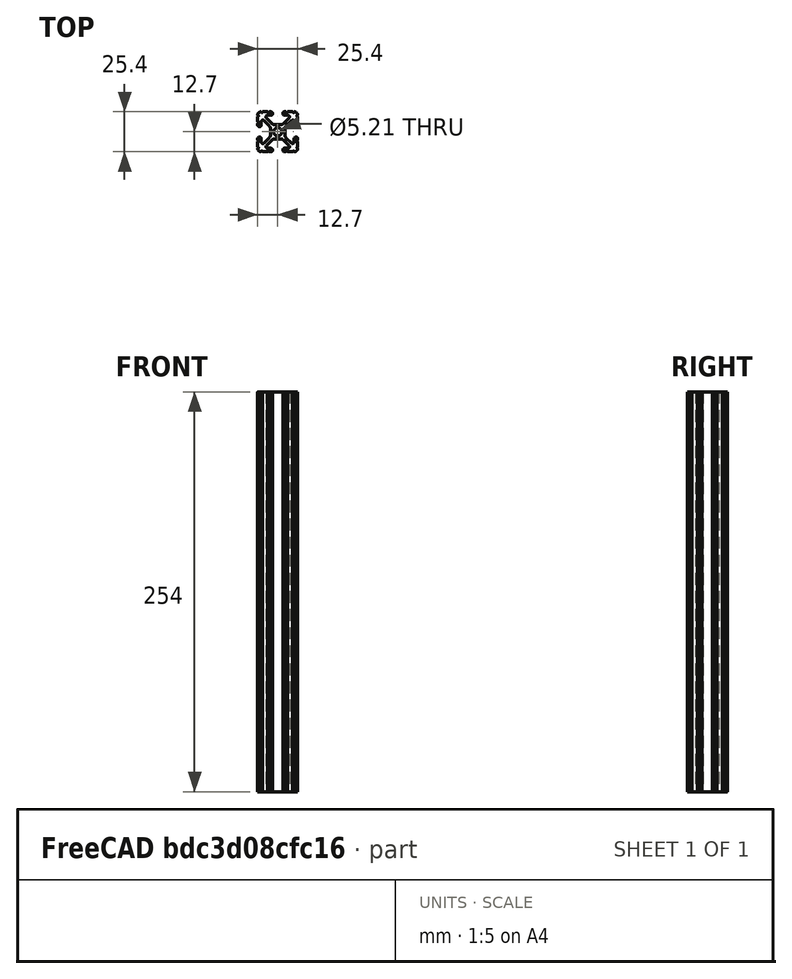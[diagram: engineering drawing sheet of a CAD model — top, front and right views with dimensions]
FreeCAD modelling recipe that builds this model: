
FCSTD DOCUMENT  (FreeCAD 0.19R23756 (Git))
Label: 1010-10
License: All rights reserved
LicenseURL: http://en.wikipedia.org/wiki/All_rights_reserved
objects: Sketcher::SketchObject×1, Part::Extrusion×1
note: 2 computed .brp shape members not serialized (recipe doc carries the construction recipe); baked Part::Feature solids carry a one-line shape summary decoded from their .brp

FEATURE [Sketcher::SketchObject] Sketch097
  FullyConstrained = false
  sketch-geometry (97):
    g0: Circle CenterX=0 CenterY=0 CenterZ=0 NormalX=0 NormalY=0 NormalZ=-1 AngleXU=0 Radius=2.6035
    g1: ArcOfCircle CenterX=12.7 CenterY=5.82508 CenterZ=0 NormalX=0 NormalY=0 NormalZ=1 AngleXU=0 Radius=0.508 StartAngle=1.5708 EndAngle=4.71239
    g2: LineSegment StartX=3.2385 StartY=11.651 StartZ=0 EndX=3.2385 EndY=11.5392 EndZ=0
    g3: LineSegment StartX=6.33313 StartY=-12.7 StartZ=0 EndX=9.55044 EndY=-12.7 EndZ=0
    g4: LineSegment StartX=7.20704 StartY=8.72437 StartZ=0 EndX=3.89827 EndY=5.42317 EndZ=0
    g5: ArcOfCircle CenterX=7.6835 CenterY=1.59319 CenterZ=0 NormalX=0 NormalY=0 NormalZ=1 AngleXU=0 Radius=3.175 StartAngle=2.35505 EndAngle=3.14159
    g6: ArcOfCircle CenterX=-1.70925 CenterY=-7.6708 CenterZ=0 NormalX=0 NormalY=0 NormalZ=1 AngleXU=0 Radius=3.175 StartAngle=1.5708 EndAngle=2.35528
    g7: ArcOfCircle CenterX=11.5392 CenterY=-4.28747 CenterZ=0 NormalX=0 NormalY=0 NormalZ=1 AngleXU=0 Radius=1.04901 StartAngle=1.5708 EndAngle=3.14159
    g8: ArcOfCircle CenterX=12.7 CenterY=-5.82508 CenterZ=0 NormalX=0 NormalY=0 NormalZ=1 AngleXU=0 Radius=0.508 StartAngle=1.5708 EndAngle=4.71239
    g9: LineSegment StartX=4.28751 StartY=10.4902 StartZ=0 EndX=6.47679 EndY=10.4902 EndZ=0
    g10: ArcOfCircle CenterX=4.28751 CenterY=11.651 CenterZ=0 NormalX=0 NormalY=0 NormalZ=1 AngleXU=0 Radius=1.04901 StartAngle=1.5708 EndAngle=3.14159
    g11: ArcOfCircle CenterX=6.47679 CenterY=9.45629 CenterZ=0 NormalX=0 NormalY=0 NormalZ=1 AngleXU=0 Radius=1.03391 StartAngle=5.49664 EndAngle=7.85398
    g12: ArcOfCircle CenterX=4.28751 CenterY=11.5392 CenterZ=0 NormalX=0 NormalY=0 NormalZ=1 AngleXU=0 Radius=1.04901 StartAngle=3.14159 EndAngle=4.71239
    g13: LineSegment StartX=3.95227 StartY=-5.42369 StartZ=0 EndX=7.17965 EndY=-8.64519 EndZ=0
    g14: ArcOfCircle CenterX=11.651 CenterY=4.28747 CenterZ=0 NormalX=0 NormalY=0 NormalZ=1 AngleXU=0 Radius=1.04901 StartAngle=4.71239 EndAngle=6.28319
    g15: ArcOfCircle CenterX=-5.82513 CenterY=-12.7 CenterZ=0 NormalX=0 NormalY=0 NormalZ=1 AngleXU=0 Radius=0.508 StartAngle=0 EndAngle=3.14159
    g16: LineSegment StartX=-6.47679 StartY=10.4902 StartZ=0 EndX=-4.28751 EndY=10.4902 EndZ=0
    g17: ArcOfCircle CenterX=-12.7 CenterY=10.0584 CenterZ=0 NormalX=0 NormalY=0 NormalZ=1 AngleXU=0 Radius=0.508 StartAngle=4.71239 EndAngle=7.85368
    g18: ArcOfCircle CenterX=-12.7 CenterY=5.82508 CenterZ=0 NormalX=0 NormalY=0 NormalZ=1 AngleXU=0 Radius=0.508 StartAngle=4.71239 EndAngle=7.85398
    g19: LineSegment StartX=-11.5392 StartY=-3.23846 StartZ=0 EndX=-11.651 EndY=-3.23846 EndZ=0
    g20: LineSegment StartX=-3.89827 StartY=5.42317 StartZ=0 EndX=-7.20704 EndY=8.72437 EndZ=0
    g21: LineSegment StartX=1.65578 StartY=4.4958 StartZ=0 EndX=-1.65578 EndY=4.4958 EndZ=0
    g22: ArcOfCircle CenterX=-1.65578 CenterY=7.6708 CenterZ=0 NormalX=0 NormalY=0 NormalZ=1 AngleXU=0 Radius=3.175 StartAngle=3.92813 EndAngle=4.71239
    g23: LineSegment StartX=-9.55044 StartY=-12.7 StartZ=0 EndX=-6.33313 EndY=-12.7 EndZ=0
    g24: ArcOfCircle CenterX=-5.82513 CenterY=12.7 CenterZ=0 NormalX=0 NormalY=0 NormalZ=1 AngleXU=0 Radius=0.508 StartAngle=3.14159 EndAngle=6.28319
    g25: ArcOfCircle CenterX=-4.28751 CenterY=11.651 CenterZ=0 NormalX=0 NormalY=0 NormalZ=1 AngleXU=0 Radius=1.04901 StartAngle=0 EndAngle=1.5708
    g26: LineSegment StartX=-12.7 StartY=-4.28747 StartZ=0 EndX=-12.7 EndY=-5.31708 EndZ=0
    g27: ArcOfCircle CenterX=-6.47679 CenterY=9.45629 CenterZ=0 NormalX=0 NormalY=0 NormalZ=1 AngleXU=0 Radius=1.03391 StartAngle=1.5708 EndAngle=3.92813
    g28: ArcOfCircle CenterX=-4.28751 CenterY=11.5392 CenterZ=0 NormalX=0 NormalY=0 NormalZ=1 AngleXU=0 Radius=1.04901 StartAngle=4.71239 EndAngle=6.28319
    g29: LineSegment StartX=-5.44101 StartY=-3.84082 StartZ=0 EndX=-8.73713 EndY=-7.12941 EndZ=0
    g30: ArcOfCircle CenterX=-7.6835 CenterY=-1.59319 CenterZ=0 NormalX=0 NormalY=0 NormalZ=1 AngleXU=0 Radius=3.175 StartAngle=5.49664 EndAngle=6.28319
    g31: LineSegment StartX=-12.7 StartY=5.31708 StartZ=0 EndX=-12.7 EndY=4.28747 EndZ=0
    g32: LineSegment StartX=-8.73713 StartY=7.12941 StartZ=0 EndX=-5.44101 EndY=3.84082 EndZ=0
    g33: LineSegment StartX=-11.651 StartY=3.23846 StartZ=0 EndX=-11.5392 EndY=3.23846 EndZ=0
    g34: ArcOfCircle CenterX=-9.46279 CenterY=-6.40209 CenterZ=0 NormalX=0 NormalY=0 NormalZ=1 AngleXU=0 Radius=1.02741 StartAngle=3.14159 EndAngle=5.49664
    g35: ArcOfCircle CenterX=-10.5918 CenterY=10.5918 CenterZ=0 NormalX=0 NormalY=0 NormalZ=1 AngleXU=0 Radius=2.1082 StartAngle=1.55877 EndAngle=3.15364
    g36: LineSegment StartX=-12.7 StartY=9.5504 StartZ=0 EndX=-12.7 EndY=6.33308 EndZ=0
    g37: LineSegment StartX=-6.33313 StartY=12.7 StartZ=0 EndX=-9.55044 EndY=12.7 EndZ=0
    g38: ArcOfCircle CenterX=-11.5392 CenterY=-4.28747 CenterZ=0 NormalX=0 NormalY=0 NormalZ=1 AngleXU=0 Radius=1.04901 StartAngle=0 EndAngle=1.5708
    g39: LineSegment StartX=4.28751 StartY=-12.7 StartZ=0 EndX=5.31713 EndY=-12.7 EndZ=0
    g40: LineSegment StartX=5.44101 StartY=3.84082 StartZ=0 EndX=8.73713 EndY=7.12941 EndZ=0
    g41: LineSegment StartX=10.4902 StartY=-4.28747 StartZ=0 EndX=10.4902 EndY=-6.40209 EndZ=0
    g42: ArcOfCircle CenterX=9.46279 CenterY=6.40209 CenterZ=0 NormalX=0 NormalY=0 NormalZ=1 AngleXU=0 Radius=1.02741 StartAngle=0 EndAngle=2.35505
    g43: ArcOfCircle CenterX=5.82513 CenterY=-12.7 CenterZ=0 NormalX=0 NormalY=0 NormalZ=1 AngleXU=0 Radius=0.508 StartAngle=0 EndAngle=3.14159
    g44: LineSegment StartX=12.7 StartY=-9.5504 StartZ=0 EndX=12.7 EndY=-6.33308 EndZ=0
    g45: LineSegment StartX=4.5085 StartY=-1.59319 StartZ=0 EndX=4.5085 EndY=1.59319 EndZ=0
    g46: ArcOfCircle CenterX=12.7 CenterY=10.0584 CenterZ=0 NormalX=0 NormalY=0 NormalZ=1 AngleXU=0 Radius=0.508 StartAngle=1.5711 EndAngle=4.71239
    g47: ArcOfCircle CenterX=12.7 CenterY=-10.0584 CenterZ=0 NormalX=0 NormalY=0 NormalZ=1 AngleXU=0 Radius=0.508 StartAngle=1.5708 EndAngle=4.71209
    g48: LineSegment StartX=3.2385 StartY=-11.5392 StartZ=0 EndX=3.2385 EndY=-11.651 EndZ=0
    g49: LineSegment StartX=8.73713 StartY=-7.12941 StartZ=0 EndX=5.44101 EndY=-3.84082 EndZ=0
    g50: ArcOfCircle CenterX=11.651 CenterY=-4.28747 CenterZ=0 NormalX=0 NormalY=0 NormalZ=1 AngleXU=0 Radius=1.04901 StartAngle=0 EndAngle=1.5708
    g51: ArcOfCircle CenterX=1.65578 CenterY=7.6708 CenterZ=0 NormalX=0 NormalY=0 NormalZ=1 AngleXU=0 Radius=3.175 StartAngle=4.71239 EndAngle=5.49664
    g52: ArcOfCircle CenterX=7.6835 CenterY=-1.59319 CenterZ=0 NormalX=0 NormalY=0 NormalZ=1 AngleXU=0 Radius=3.175 StartAngle=3.14159 EndAngle=3.92813
    g53: LineSegment StartX=12.7 StartY=4.28747 StartZ=0 EndX=12.7 EndY=5.31708 EndZ=0
    g54: ArcOfCircle CenterX=6.41641 CenterY=-9.40983 CenterZ=0 NormalX=0 NormalY=0 NormalZ=1 AngleXU=0 Radius=1.08037 StartAngle=4.71239 EndAngle=7.06949
    g55: LineSegment StartX=12.7 StartY=-5.31708 StartZ=0 EndX=12.7 EndY=-4.28747 EndZ=0
    g56: ArcOfCircle CenterX=10.0584 CenterY=-12.7 CenterZ=0 NormalX=0 NormalY=0 NormalZ=1 AngleXU=0 Radius=0.508 StartAngle=0.000300194 EndAngle=3.14159
    g57: ArcOfCircle CenterX=11.5392 CenterY=4.28747 CenterZ=0 NormalX=0 NormalY=0 NormalZ=1 AngleXU=0 Radius=1.04901 StartAngle=3.14159 EndAngle=4.71239
    g58: LineSegment StartX=12.7 StartY=6.33308 StartZ=0 EndX=12.7 EndY=9.5504 EndZ=0
    g59: ArcOfCircle CenterX=4.28751 CenterY=-11.5392 CenterZ=0 NormalX=0 NormalY=0 NormalZ=1 AngleXU=0 Radius=1.04901 StartAngle=1.5708 EndAngle=3.14159
    g60: ArcOfCircle CenterX=10.5918 CenterY=10.5918 CenterZ=0 NormalX=0 NormalY=0 NormalZ=1 AngleXU=0 Radius=2.1082 StartAngle=6.27114 EndAngle=7.86601
    g61: ArcOfCircle CenterX=9.46279 CenterY=-6.40209 CenterZ=0 NormalX=0 NormalY=0 NormalZ=1 AngleXU=0 Radius=1.02741 StartAngle=3.92813 EndAngle=6.28319
    g62: LineSegment StartX=6.41641 StartY=-10.4902 StartZ=0 EndX=4.28751 EndY=-10.4902 EndZ=0
    g63: LineSegment StartX=-10.4902 StartY=-6.40209 StartZ=0 EndX=-10.4902 EndY=-4.28747 EndZ=0
    g64: ArcOfCircle CenterX=-9.46279 CenterY=6.40209 CenterZ=0 NormalX=0 NormalY=0 NormalZ=1 AngleXU=0 Radius=1.02741 StartAngle=0.786542 EndAngle=3.14159
    g65: LineSegment StartX=-10.4902 StartY=4.28747 StartZ=0 EndX=-10.4902 EndY=6.40209 EndZ=0
    g66: LineSegment StartX=-4.5085 StartY=1.59319 StartZ=0 EndX=-4.5085 EndY=-1.59319 EndZ=0
    g67: LineSegment StartX=-4.28751 StartY=12.7 StartZ=0 EndX=-5.31713 EndY=12.7 EndZ=0
    g68: ArcOfCircle CenterX=-11.5392 CenterY=4.28747 CenterZ=0 NormalX=0 NormalY=0 NormalZ=1 AngleXU=0 Radius=1.04901 StartAngle=4.71239 EndAngle=6.28319
    g69: LineSegment StartX=-3.2385 StartY=11.5392 StartZ=0 EndX=-3.2385 EndY=11.651 EndZ=0
    g70: ArcOfCircle CenterX=-11.651 CenterY=4.28747 CenterZ=0 NormalX=0 NormalY=0 NormalZ=1 AngleXU=0 Radius=1.04901 StartAngle=3.14159 EndAngle=4.71239
    g71: ArcOfCircle CenterX=-7.6835 CenterY=1.59319 CenterZ=0 NormalX=0 NormalY=0 NormalZ=1 AngleXU=0 Radius=3.175 StartAngle=0 EndAngle=0.786542
    g72: ArcOfCircle CenterX=-10.0584 CenterY=12.7 CenterZ=0 NormalX=0 NormalY=0 NormalZ=1 AngleXU=0 Radius=0.508 StartAngle=3.14189 EndAngle=6.28319
    g73: LineSegment StartX=-1.70925 StartY=-4.4958 StartZ=0 EndX=1.70925 EndY=-4.4958 EndZ=0
    g74: LineSegment StartX=11.651 StartY=-3.23846 StartZ=0 EndX=11.5392 EndY=-3.23846 EndZ=0
    g75: ArcOfCircle CenterX=-10.5918 CenterY=-10.5918 CenterZ=0 NormalX=0 NormalY=0 NormalZ=1 AngleXU=0 Radius=2.1082 StartAngle=3.12954 EndAngle=4.72442
    g76: ArcOfCircle CenterX=10.5918 CenterY=-10.5918 CenterZ=0 NormalX=0 NormalY=0 NormalZ=1 AngleXU=0 Radius=2.1082 StartAngle=4.70036 EndAngle=6.29523
    g77: ArcOfCircle CenterX=-12.7 CenterY=-5.82508 CenterZ=0 NormalX=0 NormalY=0 NormalZ=1 AngleXU=0 Radius=0.508 StartAngle=4.71239 EndAngle=7.85398
    g78: ArcOfCircle CenterX=5.82513 CenterY=12.7 CenterZ=0 NormalX=0 NormalY=0 NormalZ=1 AngleXU=0 Radius=0.508 StartAngle=3.14159 EndAngle=6.28319
    g79: LineSegment StartX=9.55044 StartY=12.7 StartZ=0 EndX=6.33313 EndY=12.7 EndZ=0
    g80: ArcOfCircle CenterX=10.0584 CenterY=12.7 CenterZ=0 NormalX=0 NormalY=0 NormalZ=1 AngleXU=0 Radius=0.508 StartAngle=3.14159 EndAngle=6.28289
    g81: ArcOfCircle CenterX=1.70925 CenterY=-7.6708 CenterZ=0 NormalX=0 NormalY=0 NormalZ=1 AngleXU=0 Radius=3.175 StartAngle=0.78631 EndAngle=1.5708
    g82: ArcOfCircle CenterX=4.28751 CenterY=-11.651 CenterZ=0 NormalX=0 NormalY=0 NormalZ=1 AngleXU=0 Radius=1.04901 StartAngle=3.14159 EndAngle=4.71239
    g83: LineSegment StartX=5.31713 StartY=12.7 StartZ=0 EndX=4.28751 EndY=12.7 EndZ=0
    g84: LineSegment StartX=10.4902 StartY=6.40209 StartZ=0 EndX=10.4902 EndY=4.28747 EndZ=0
    g85: LineSegment StartX=11.5392 StartY=3.23846 StartZ=0 EndX=11.651 EndY=3.23846 EndZ=0
    g86: ArcOfCircle CenterX=-10.0584 CenterY=-12.7 CenterZ=0 NormalX=0 NormalY=0 NormalZ=1 AngleXU=0 Radius=0.508 StartAngle=0 EndAngle=3.14129
    g87: ArcOfCircle CenterX=-12.7 CenterY=-10.0584 CenterZ=0 NormalX=0 NormalY=0 NormalZ=1 AngleXU=0 Radius=0.508 StartAngle=4.71269 EndAngle=7.85398
    g88: ArcOfCircle CenterX=-4.28751 CenterY=-11.5392 CenterZ=0 NormalX=0 NormalY=0 NormalZ=1 AngleXU=0 Radius=1.04901 StartAngle=0 EndAngle=1.5708
    g89: ArcOfCircle CenterX=-4.28751 CenterY=-11.651 CenterZ=0 NormalX=0 NormalY=0 NormalZ=1 AngleXU=0 Radius=1.04901 StartAngle=4.71239 EndAngle=6.28319
    g90: LineSegment StartX=-12.7 StartY=-6.33308 StartZ=0 EndX=-12.7 EndY=-9.5504 EndZ=0
    g91: ArcOfCircle CenterX=-11.651 CenterY=-4.28747 CenterZ=0 NormalX=0 NormalY=0 NormalZ=1 AngleXU=0 Radius=1.04901 StartAngle=1.5708 EndAngle=3.14159
    g92: LineSegment StartX=-7.17965 StartY=-8.64519 StartZ=0 EndX=-3.95227 EndY=-5.42369 EndZ=0
    g93: LineSegment StartX=-5.31713 StartY=-12.7 StartZ=0 EndX=-4.28751 EndY=-12.7 EndZ=0
    g94: LineSegment StartX=-3.2385 StartY=-11.651 StartZ=0 EndX=-3.2385 EndY=-11.5392 EndZ=0
    g95: ArcOfCircle CenterX=-6.41641 CenterY=-9.40983 CenterZ=0 NormalX=0 NormalY=0 NormalZ=1 AngleXU=0 Radius=1.08037 StartAngle=2.35528 EndAngle=4.71239
    g96: LineSegment StartX=-4.28751 StartY=-10.4902 StartZ=0 EndX=-6.41641 EndY=-10.4902 EndZ=0
FEATURE [Part::Extrusion] Extrude
  Base = -> Sketch097
  Dir = (0,0,1)
  DirMode = 2
  FaceMakerClass = Part::FaceMakerBullseye
  LengthFwd = 254
  LengthRev = 0
  Solid = true
  Symmetric = false
